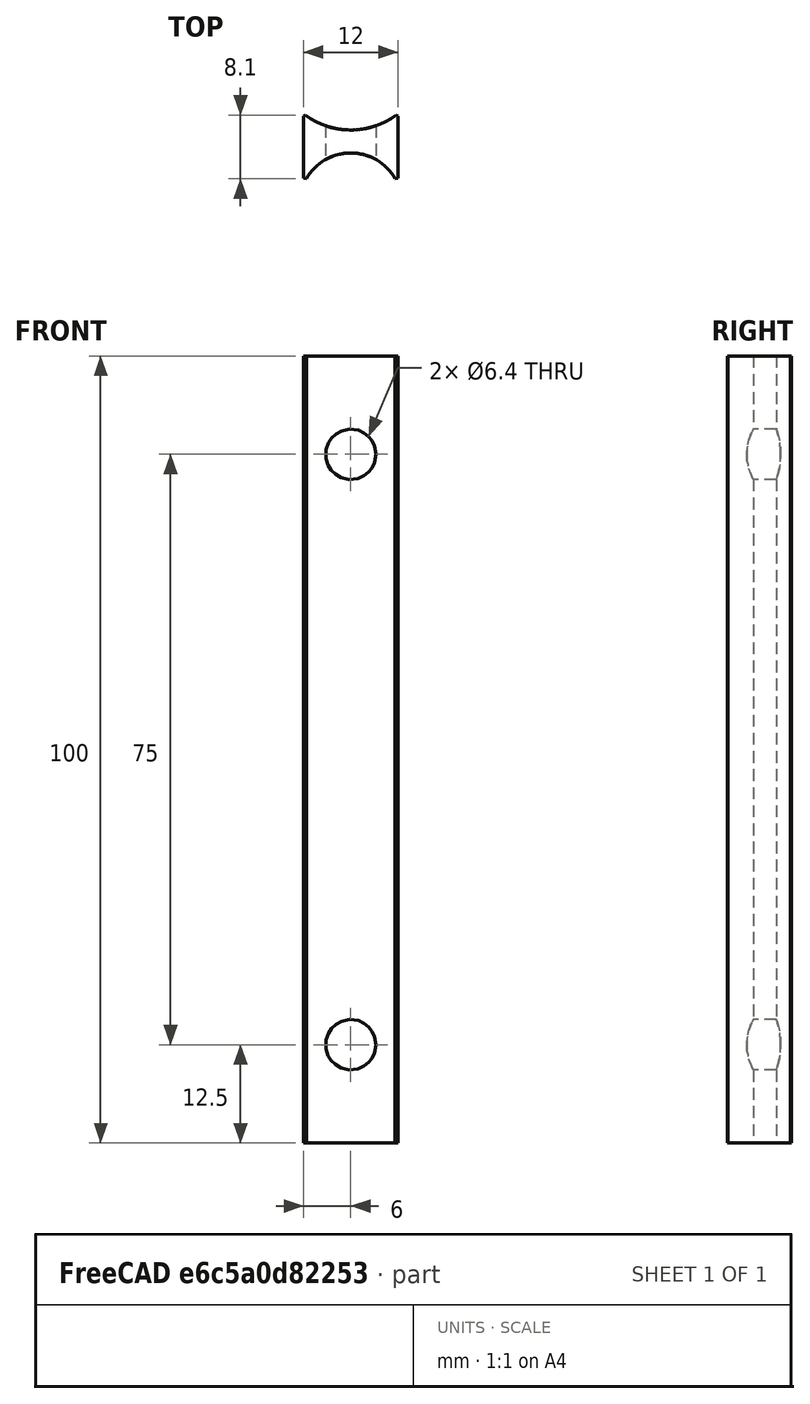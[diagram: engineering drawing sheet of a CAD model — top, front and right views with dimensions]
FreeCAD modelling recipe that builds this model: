
FCSTD DOCUMENT  (FreeCAD 0.16R)
Label: Cargispacer
License: All rights reserved
LicenseURL: http://en.wikipedia.org/wiki/All_rights_reserved
objects: Sketcher::SketchObject×2, Part::Cylinder×2, Part::Cut×2, PartDesign::Chamfer×2, PartDesign::Pad×1, Mesh::Feature×1
note: 10 computed .brp shape members not serialized (recipe doc carries the construction recipe); baked Part::Feature solids carry a one-line shape summary decoded from their .brp

FEATURE [Sketcher::SketchObject] Sketch
FEATURE [Sketcher::SketchObject] Sketch001
  sketch-geometry (4):
    g0: ArcOfCircle CenterX=0 CenterY=7.62168 CenterZ=0 NormalX=0 NormalY=0 NormalZ=1 Radius=9.7 StartAngle=4.04548 EndAngle=5.37929
    g1: ArcOfCircle CenterX=-1e-12 CenterY=-11.5 CenterZ=0 NormalX=0 NormalY=0 NormalZ=1 Radius=6.5 StartAngle=0.394791 EndAngle=2.7468
    g2: LineSegment StartX=-6 StartY=0 StartZ=0 EndX=-6 EndY=-9 EndZ=0
    g3: LineSegment StartX=6 StartY=0 StartZ=0 EndX=6 EndY=-9 EndZ=0
  constraints (13):
    c: PointOnObject(g0,g-2)
    c: Radius(g1) = 6.5
    c: Radius(g0) = 9.7
    c: Coincident(g2,g0)
    c: Coincident(g2,g1)
    c: Coincident(g3,g0)
    c: Coincident(g3,g1)
    c: Equal(g2,g3)
    c: Distance(g0,g0) = 12
    c: Symmetric(g1,g1,g-2)
    c: Distance(g1,g1) = 12
    c: Distance(g3) = 9
    c: PointOnObject(g0,g-1)
FEATURE [PartDesign::Pad] Pad
  Length = 100
  Length2 = 100
  Midplane = true
  Sketch = -> Sketch001
  Type = 0
FEATURE [Part::Cylinder] Cylinder
  Angle = 360
  Height = 10
  Placement = pos=(0,0,37.5) rot=(1,0,0;1.5708rad)
  Radius = 3.2
FEATURE [Part::Cut] Cut
  Base = -> Pad
  Tool = -> Cylinder
FEATURE [Part::Cylinder] Cylinder001
  Angle = 360
  Height = 10
  Placement = pos=(0,0,-37.5) rot=(1,0,0;1.5708rad)
  Radius = 3.2
FEATURE [Part::Cut] Cut001
  Base = -> Cut
  Tool = -> Cylinder001
FEATURE [PartDesign::Chamfer] Chamfer
  Base = -> Cut001 [Edge7,Edge14]
  Size = 0.8
FEATURE [PartDesign::Chamfer] Chamfer001
  Base = -> Chamfer [Edge3,Edge13]
  Size = 0.3
FEATURE [Mesh::Feature] Mesh  label="Chamfer001 (Meshed)"
